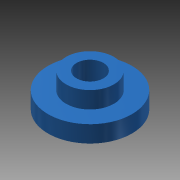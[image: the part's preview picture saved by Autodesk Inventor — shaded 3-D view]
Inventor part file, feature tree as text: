
AUTODESK INVENTOR PART (.ipt)
format: ipt  version: 2013 SP2 (Build 170200200, 200)  size: 87,040 bytes
history: native  units: mm
features: extrude x2, sketch x2
ambient origin geometry x8: Origin, YZ Plane, XZ Plane, XY Plane, X Axis, Y Axis, Z Axis, Center Point
bodies: Solid1 (feature_tree)
feature tree (4):
  extrude  "Extrusion1"  Depth=10.0mm
  extrude  "Extrusion2"  Depth=5.7mm
  sketch  "Sketch1"  dims[d0=3.2mm d1=10.0mm]
  sketch  "Sketch2"  dims[d2=2.0mm d3=0.0mm d4=5.7mm d5=2.0mm d6=0.0mm]
